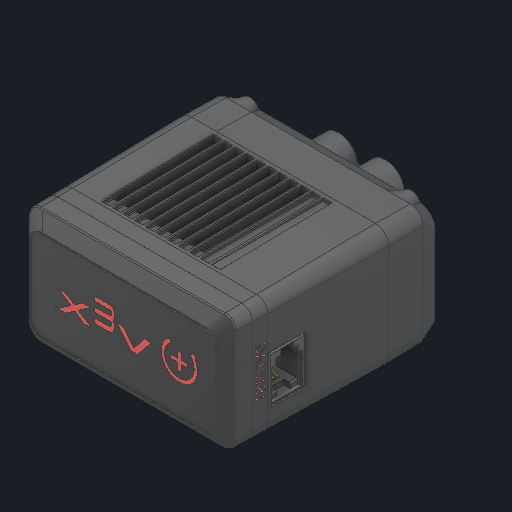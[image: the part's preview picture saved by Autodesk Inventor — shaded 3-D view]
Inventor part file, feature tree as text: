
AUTODESK INVENTOR PART (.ipt)
format: ipt  version: 2024 (Build 280153000, 153)  size: 13,033,984 bytes
history: native  units: in
note: dims shown in document units (in); Inventor stores cm internally (conversion verified against a paired STEP export)
features: other x19, sketch x2
ambient origin geometry x8: Origin, YZ Plane, XZ Plane, XY Plane, X Axis, Y Axis, Z Axis, Center Point
bodies: Solid1 (feature_tree), Solid2 (feature_tree), Solid7 (feature_tree), Solid8 (feature_tree), Solid9 (feature_tree), Solid20 (feature_tree), Solid21 (feature_tree), Solid22 (feature_tree)
feature tree (21):
  other  "V5 Motor.ipt"
  other  "Solid1::V5 Motor.ipt"
  other  "Solid2::V5 Motor.ipt"
  other  "Solid4::V5 Motor.ipt"
  other  "Solid6::V5 Motor.ipt"
  other  "Solid7::V5 Motor.ipt"
  other  "Solid8::V5 Motor.ipt"
  other  "Solid9::V5 Motor.ipt"
  other  "Solid14::V5 Motor.ipt"
  other  "Solid16::V5 Motor.ipt"
  other  "Solid17::V5 Motor.ipt"
  other  "Solid18::V5 Motor.ipt"
  other  "Solid19::V5 Motor.ipt"
  other  "Solid20::V5 Motor.ipt"
  other  "Solid21::V5 Motor.ipt"
  other  "Solid22::V5 Motor.ipt"
  other  "TaggingFeature1"
  sketch  "Sketch1"  dims[d0=0.3937in]
  sketch  "Sketch2"  dims[d4=0.0in d5=0.0in]
  other  "iInsert:1"
  other  "iInsert:2"
